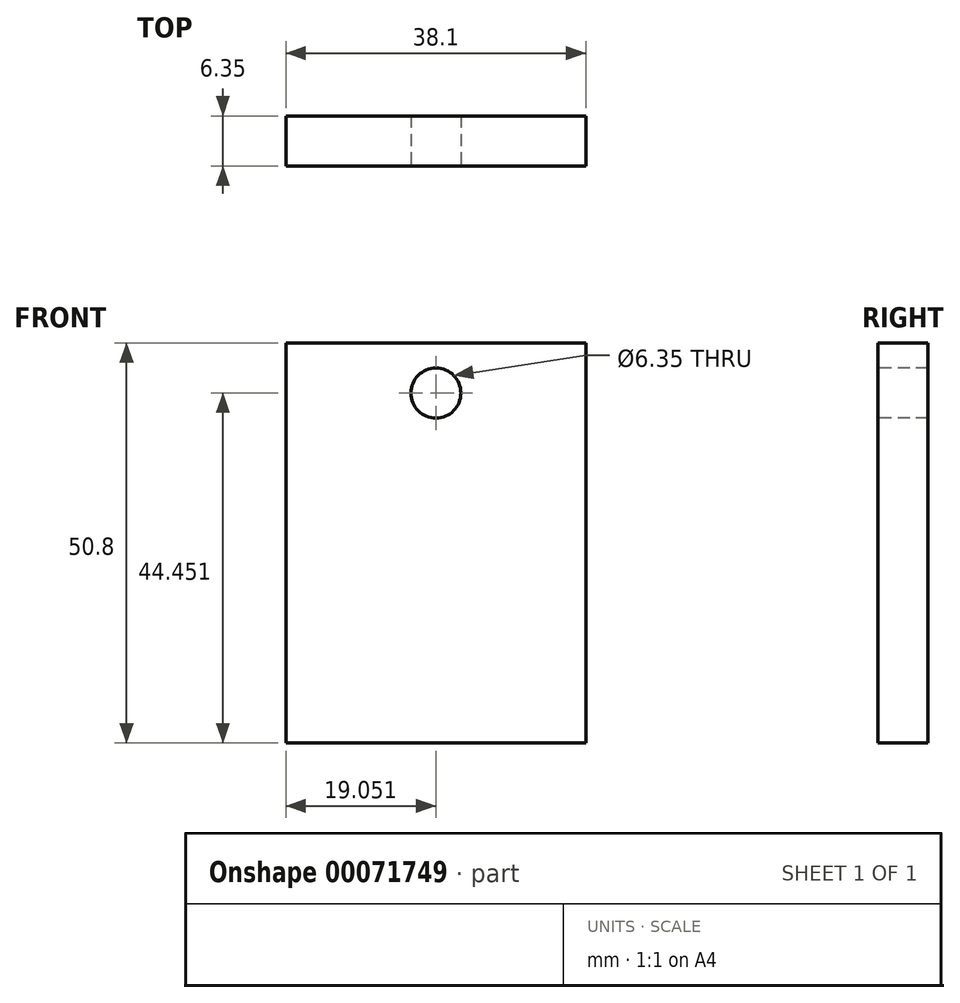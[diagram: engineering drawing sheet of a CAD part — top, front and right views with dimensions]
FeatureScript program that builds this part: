
annotation { "Feature Type Name" : "Feature", "Feature Type Description" : "" }
export const myFeature = defineFeature(function(context is Context, id is Id, definition is map)
    precondition{}
    {
        {
            var Q0;
            Q0=qCreatedBy(makeId("Front.planeOp"),FACE);
            var sketch = newSketch(context, id + "F0", { "sketchPlane" : qUnion([Q0])});
            skLineSegment(sketch, "E0.bottom", {"start": v(-74.78, -24.2) * mm, "end": v(-36.68, -24.2) * mm});
            skLineSegment(sketch, "E0.top", {"start": v(-74.78, -75) * mm, "end": v(-36.68, -75) * mm});
            skLineSegment(sketch, "E0.left", {"start": v(-74.78, -24.2) * mm, "end": v(-74.78, -75) * mm});
            skLineSegment(sketch, "E0.right", {"start": v(-36.68, -24.2) * mm, "end": v(-36.68, -75) * mm});
            skSolve(sketch);
        }
        {
            var Q0;
            Q0 = qSketchRegion(id + "F0", true);
            extrude(context, id + "F1", {"entities" : qUnion([Q0]), "depth" : 6.35 * mm});
        }
        {
            var Q0;
            Q0=makeQuery(id+"F1.opExtrude","CAP_FACE",FACE,{"disambiguationData":[OSD([sQuery(id+"F0.wireOp",EDGE,"E0.bottom"),sQuery(id+"F0.wireOp",EDGE,"E0.top"),sQuery(id+"F0.wireOp",EDGE,"E0.left"),sQuery(id+"F0.wireOp",EDGE,"E0.right")])],"isStart":false});
            var sketch = newSketch(context, id + "F2", { "sketchPlane" : qUnion([Q0])});
            skLineSegment(sketch, "E1", {"start": v(-55.73, -24.2) * mm, "end": v(-55.73, -75) * mm, "construction": true});
            skLineSegment(sketch, "E2", {"start": v(-74.78, -30.56) * mm, "end": v(-36.68, -30.56) * mm, "construction": true});
            skCircle(sketch, "E3", {"center": v(-55.73, -30.56) * mm, "radius": 3.18 * mm});
            skSolve(sketch);
        }
        {
            var Q0;
            Q0 = qSketchRegion(id + "F2", true);
            extrude(context, id + "F3", {"entities" : qUnion([Q0]), "operationType" : NewBodyOperationType.REMOVE, "oppositeDirection" : true, "depth" : 25.4 * mm});
        }
    });
